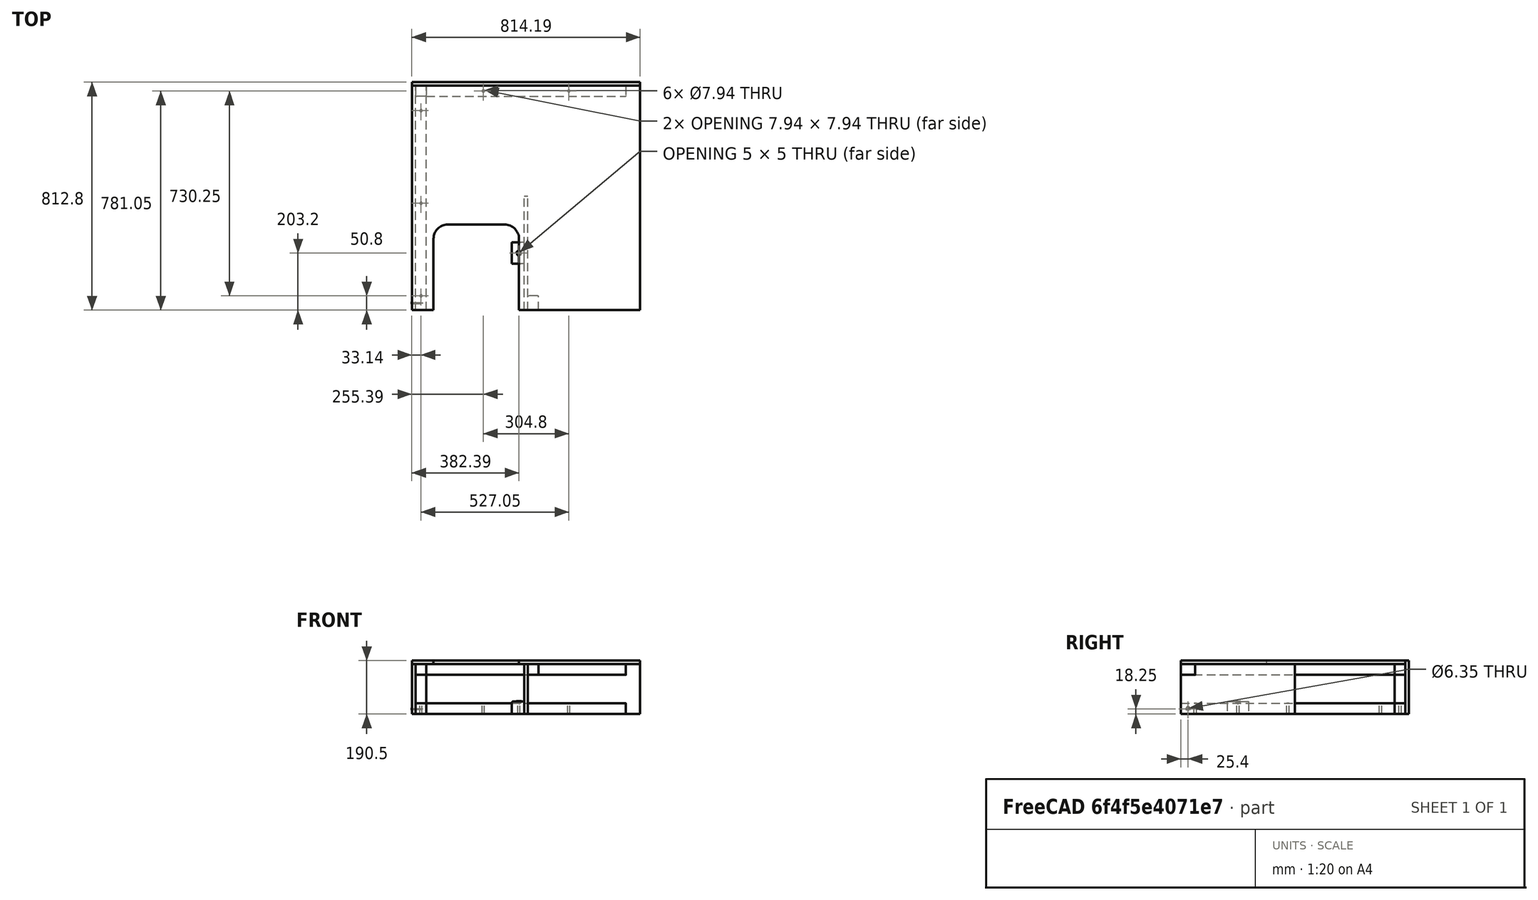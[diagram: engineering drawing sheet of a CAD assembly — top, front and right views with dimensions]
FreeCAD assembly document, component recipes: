
FREECAD ASSEMBLY — COMPONENT RECIPES ("Baffle_Box")

This assembly document has 66 components, labeled P0..P65 below (a component is one placed body or linked part). 0 of them carry a construction recipe — the FreeCAD feature program that regenerates the part from scratch, quoted from this document or its linked companion documents; the rest are supplied as boundary geometry only. No exploded tour is included for this assembly.
COMPONENT P0 — geometry summary ("Screw_w_Washer_A001"; no construction recipe available for this part):
  bounding box: 38.1 x 15.9 x 15.9 mm
  tessellated surface: 2,492 triangles
  volume: 527 mm^3 (5% of its bounding box)
  symmetry: mirror-symmetric across its y mid-plane, z mid-plane
COMPONENT P1 — geometry summary ("Part_F_Baffle_Side_Wall_002"; no construction recipe available for this part):
  bounding box: 800.1 x 177.8 x 12.7 mm
  tessellated surface: 12 triangles
  volume: 1806674 mm^3 (100% of its bounding box)
  symmetry: 2-fold rotationally symmetric about the x axis; 2-fold rotationally symmetric about the y axis; 2-fold rotationally symmetric about the z axis; mirror-symmetric across its x mid-plane, y mid-plane, z mid-plane
COMPONENT P2 — geometry summary ("BF_A001"; no construction recipe available for this part):
  bounding box: 800.1 x 38.1 x 38.1 mm
  tessellated surface: 220 triangles
  volume: 1154510 mm^3 (99% of its bounding box)
  symmetry: 2-fold rotationally symmetric about the x axis; 4-fold rotationally symmetric about the y axis; 2-fold rotationally symmetric about the z axis; mirror-symmetric across its x mid-plane, z mid-plane
COMPONENT P3 — geometry summary ("BF_B001"; no construction recipe available for this part):
  bounding box: 711.2 x 38.1 x 38.1 mm
  tessellated surface: 220 triangles
  volume: 1026231 mm^3 (99% of its bounding box)
  symmetry: 2-fold rotationally symmetric about the x axis; 2-fold rotationally symmetric about the y axis; 2-fold rotationally symmetric about the z axis; mirror-symmetric across its y mid-plane, z mid-plane
COMPONENT P4 — geometry summary ("BF_C001"; no construction recipe available for this part):
  bounding box: 139.7 x 38.1 x 38.1 mm
  tessellated surface: 220 triangles
  volume: 201581 mm^3 (99% of its bounding box)
  symmetry: 2-fold rotationally symmetric about the y axis; 4-fold rotationally symmetric about the z axis; mirror-symmetric across its y mid-plane, z mid-plane
COMPONENT P5 — geometry summary ("BF_E001"; no construction recipe available for this part):
  bounding box: 50.8 x 38.1 x 38.1 mm
  tessellated surface: 220 triangles
  volume: 73302 mm^3 (99% of its bounding box)
  symmetry: 4-fold rotationally symmetric about the y axis; 2-fold rotationally symmetric about the z axis; mirror-symmetric across its x mid-plane, y mid-plane
COMPONENT P6 — geometry summary ("Screw_w_Washer_A002"; no construction recipe available for this part):
  bounding box: 38.1 x 15.9 x 15.9 mm
  tessellated surface: 2,492 triangles
  volume: 527 mm^3 (5% of its bounding box)
  symmetry: mirror-symmetric across its y mid-plane, z mid-plane
COMPONENT P7 — geometry summary ("Screw_w_Washer_A003"; no construction recipe available for this part):
  bounding box: 38.1 x 15.9 x 15.9 mm
  tessellated surface: 2,492 triangles
  volume: 527 mm^3 (5% of its bounding box)
  symmetry: mirror-symmetric across its y mid-plane, z mid-plane
COMPONENT P8 — geometry summary ("Screw_w_Washer_A004"; no construction recipe available for this part):
  bounding box: 38.1 x 15.9 x 15.9 mm
  tessellated surface: 2,492 triangles
  volume: 527 mm^3 (5% of its bounding box)
  symmetry: mirror-symmetric across its y mid-plane, z mid-plane
COMPONENT P9 — geometry summary ("Screw_w_Washer_A005"; no construction recipe available for this part):
  bounding box: 38.1 x 15.9 x 15.9 mm
  tessellated surface: 2,492 triangles
  volume: 527 mm^3 (5% of its bounding box)
  symmetry: mirror-symmetric across its y mid-plane, z mid-plane
COMPONENT P10 — geometry summary ("Screw_w_Washer_A006"; no construction recipe available for this part):
  bounding box: 38.1 x 15.9 x 15.9 mm
  tessellated surface: 2,492 triangles
  volume: 527 mm^3 (5% of its bounding box)
  symmetry: mirror-symmetric across its y mid-plane, z mid-plane
COMPONENT P11 — geometry summary ("Screw_w_Washer_A007"; no construction recipe available for this part):
  bounding box: 38.1 x 15.9 x 15.9 mm
  tessellated surface: 2,492 triangles
  volume: 527 mm^3 (5% of its bounding box)
  symmetry: mirror-symmetric across its y mid-plane, z mid-plane
COMPONENT P12 — geometry summary ("Screw_w_Washer_A008"; no construction recipe available for this part):
  bounding box: 38.1 x 15.9 x 15.9 mm
  tessellated surface: 2,492 triangles
  volume: 527 mm^3 (5% of its bounding box)
  symmetry: mirror-symmetric across its y mid-plane, z mid-plane
COMPONENT P13 — geometry summary ("Screw_w_Washer_A009"; no construction recipe available for this part):
  bounding box: 38.1 x 15.9 x 15.9 mm
  tessellated surface: 2,492 triangles
  volume: 527 mm^3 (5% of its bounding box)
  symmetry: mirror-symmetric across its y mid-plane, z mid-plane
COMPONENT P14 — geometry summary ("Screw_w_Washer_A010"; no construction recipe available for this part):
  bounding box: 38.1 x 15.9 x 15.9 mm
  tessellated surface: 2,492 triangles
  volume: 527 mm^3 (5% of its bounding box)
  symmetry: mirror-symmetric across its y mid-plane, z mid-plane
COMPONENT P15 — geometry summary ("Screw_w_Washer_A011"; no construction recipe available for this part):
  bounding box: 38.1 x 15.9 x 15.9 mm
  tessellated surface: 2,492 triangles
  volume: 527 mm^3 (5% of its bounding box)
  symmetry: mirror-symmetric across its y mid-plane, z mid-plane
COMPONENT P16 — geometry summary ("Screw_w_Washer_A012"; no construction recipe available for this part):
  bounding box: 38.1 x 15.9 x 15.9 mm
  tessellated surface: 2,492 triangles
  volume: 527 mm^3 (5% of its bounding box)
  symmetry: mirror-symmetric across its y mid-plane, z mid-plane
COMPONENT P17 — geometry summary ("Screw_w_Washer_A013"; no construction recipe available for this part):
  bounding box: 38.1 x 15.9 x 15.9 mm
  tessellated surface: 2,492 triangles
  volume: 527 mm^3 (5% of its bounding box)
  symmetry: mirror-symmetric across its y mid-plane, z mid-plane
COMPONENT P18 — geometry summary ("Screw_w_Washer_A014"; no construction recipe available for this part):
  bounding box: 38.1 x 15.9 x 15.9 mm
  tessellated surface: 2,492 triangles
  volume: 527 mm^3 (5% of its bounding box)
  symmetry: mirror-symmetric across its y mid-plane, z mid-plane
COMPONENT P19 — geometry summary ("Screw_w_Washer_A015"; no construction recipe available for this part):
  bounding box: 38.1 x 15.9 x 15.9 mm
  tessellated surface: 2,492 triangles
  volume: 527 mm^3 (5% of its bounding box)
  symmetry: mirror-symmetric across its y mid-plane, z mid-plane
COMPONENT P20 — geometry summary ("Screw_w_Washer_A016"; no construction recipe available for this part):
  bounding box: 38.1 x 15.9 x 15.9 mm
  tessellated surface: 2,492 triangles
  volume: 527 mm^3 (5% of its bounding box)
  symmetry: mirror-symmetric across its y mid-plane, z mid-plane
COMPONENT P21 — geometry summary ("Screw_w_Washer_A017"; no construction recipe available for this part):
  bounding box: 38.1 x 15.9 x 15.9 mm
  tessellated surface: 2,492 triangles
  volume: 527 mm^3 (5% of its bounding box)
  symmetry: mirror-symmetric across its y mid-plane, z mid-plane
COMPONENT P22 — geometry summary ("Screw_w_Washer_A018"; no construction recipe available for this part):
  bounding box: 38.1 x 15.9 x 15.9 mm
  tessellated surface: 2,492 triangles
  volume: 527 mm^3 (5% of its bounding box)
  symmetry: mirror-symmetric across its y mid-plane, z mid-plane
COMPONENT P23 — geometry summary ("Screw_w_Washer_A019"; no construction recipe available for this part):
  bounding box: 38.1 x 15.9 x 15.9 mm
  tessellated surface: 2,492 triangles
  volume: 527 mm^3 (5% of its bounding box)
  symmetry: mirror-symmetric across its y mid-plane, z mid-plane
COMPONENT P24 — geometry summary ("Screw_w_Washer_A020"; no construction recipe available for this part):
  bounding box: 38.1 x 15.9 x 15.9 mm
  tessellated surface: 2,492 triangles
  volume: 527 mm^3 (5% of its bounding box)
  symmetry: mirror-symmetric across its y mid-plane, z mid-plane
COMPONENT P25 — geometry summary ("Screw_w_Washer_A021"; no construction recipe available for this part):
  bounding box: 38.1 x 15.9 x 15.9 mm
  tessellated surface: 2,492 triangles
  volume: 527 mm^3 (5% of its bounding box)
  symmetry: mirror-symmetric across its y mid-plane, z mid-plane
COMPONENT P26 — geometry summary ("Screw_w_Washer_A022"; no construction recipe available for this part):
  bounding box: 38.1 x 15.9 x 15.9 mm
  tessellated surface: 2,492 triangles
  volume: 527 mm^3 (5% of its bounding box)
  symmetry: mirror-symmetric across its y mid-plane, z mid-plane
COMPONENT P27 — geometry summary ("Screw_w_Washer_A023"; no construction recipe available for this part):
  bounding box: 38.1 x 15.9 x 15.9 mm
  tessellated surface: 2,492 triangles
  volume: 527 mm^3 (5% of its bounding box)
  symmetry: mirror-symmetric across its y mid-plane, z mid-plane
COMPONENT P28 — geometry summary ("Screw_w_Washer_A024"; no construction recipe available for this part):
  bounding box: 38.1 x 15.9 x 15.9 mm
  tessellated surface: 2,492 triangles
  volume: 527 mm^3 (5% of its bounding box)
  symmetry: mirror-symmetric across its y mid-plane, z mid-plane
COMPONENT P29 — geometry summary ("Screw_w_Washer_A025"; no construction recipe available for this part):
  bounding box: 38.1 x 15.9 x 15.9 mm
  tessellated surface: 2,492 triangles
  volume: 527 mm^3 (5% of its bounding box)
  symmetry: mirror-symmetric across its y mid-plane, z mid-plane
COMPONENT P30 — geometry summary ("Screw_w_Washer_A026"; no construction recipe available for this part):
  bounding box: 38.1 x 15.9 x 15.9 mm
  tessellated surface: 2,492 triangles
  volume: 527 mm^3 (5% of its bounding box)
  symmetry: mirror-symmetric across its y mid-plane, z mid-plane
COMPONENT P31 — geometry summary ("Screw_w_Washer_A027"; no construction recipe available for this part):
  bounding box: 38.1 x 15.9 x 15.9 mm
  tessellated surface: 2,492 triangles
  volume: 527 mm^3 (5% of its bounding box)
  symmetry: mirror-symmetric across its y mid-plane, z mid-plane
COMPONENT P32 — geometry summary ("Screw_w_Washer_A028"; no construction recipe available for this part):
  bounding box: 38.1 x 15.9 x 15.9 mm
  tessellated surface: 2,492 triangles
  volume: 527 mm^3 (5% of its bounding box)
  symmetry: mirror-symmetric across its y mid-plane, z mid-plane
COMPONENT P33 — geometry summary ("Screw_w_Washer_A029"; no construction recipe available for this part):
  bounding box: 38.1 x 15.9 x 15.9 mm
  tessellated surface: 2,492 triangles
  volume: 527 mm^3 (5% of its bounding box)
  symmetry: mirror-symmetric across its y mid-plane, z mid-plane
COMPONENT P34 — geometry summary ("Screw_w_Washer_A030"; no construction recipe available for this part):
  bounding box: 38.1 x 15.9 x 15.9 mm
  tessellated surface: 2,492 triangles
  volume: 527 mm^3 (5% of its bounding box)
  symmetry: mirror-symmetric across its y mid-plane, z mid-plane
COMPONENT P35 — geometry summary ("Screw_w_Washer_A031"; no construction recipe available for this part):
  bounding box: 38.1 x 15.9 x 15.9 mm
  tessellated surface: 2,492 triangles
  volume: 527 mm^3 (5% of its bounding box)
  symmetry: mirror-symmetric across its y mid-plane, z mid-plane
COMPONENT P36 — geometry summary ("Screw_w_Washer_A032"; no construction recipe available for this part):
  bounding box: 38.1 x 15.9 x 15.9 mm
  tessellated surface: 2,492 triangles
  volume: 527 mm^3 (5% of its bounding box)
  symmetry: mirror-symmetric across its y mid-plane, z mid-plane
COMPONENT P37 — geometry summary ("Screw_w_Washer_A033"; no construction recipe available for this part):
  bounding box: 38.1 x 15.9 x 15.9 mm
  tessellated surface: 2,492 triangles
  volume: 527 mm^3 (5% of its bounding box)
  symmetry: mirror-symmetric across its y mid-plane, z mid-plane
COMPONENT P38 — geometry summary ("Screw_w_Washer_A034"; no construction recipe available for this part):
  bounding box: 38.1 x 15.9 x 15.9 mm
  tessellated surface: 2,492 triangles
  volume: 527 mm^3 (5% of its bounding box)
  symmetry: mirror-symmetric across its y mid-plane, z mid-plane
COMPONENT P39 — geometry summary ("Screw_w_Washer_A035"; no construction recipe available for this part):
  bounding box: 38.1 x 15.9 x 15.9 mm
  tessellated surface: 2,492 triangles
  volume: 527 mm^3 (5% of its bounding box)
  symmetry: mirror-symmetric across its y mid-plane, z mid-plane
COMPONENT P40 — geometry summary ("Screw_w_Washer_A036"; no construction recipe available for this part):
  bounding box: 38.1 x 15.9 x 15.9 mm
  tessellated surface: 2,492 triangles
  volume: 527 mm^3 (5% of its bounding box)
  symmetry: mirror-symmetric across its y mid-plane, z mid-plane
COMPONENT P41 — geometry summary ("Screw_w_Washer_A037"; no construction recipe available for this part):
  bounding box: 38.1 x 15.9 x 15.9 mm
  tessellated surface: 2,492 triangles
  volume: 527 mm^3 (5% of its bounding box)
  symmetry: mirror-symmetric across its y mid-plane, z mid-plane
COMPONENT P42 — geometry summary ("Screw_w_Washer_A038"; no construction recipe available for this part):
  bounding box: 38.1 x 15.9 x 15.9 mm
  tessellated surface: 2,492 triangles
  volume: 527 mm^3 (5% of its bounding box)
  symmetry: mirror-symmetric across its y mid-plane, z mid-plane
COMPONENT P43 — geometry summary ("Screw_w_Washer_A039"; no construction recipe available for this part):
  bounding box: 38.1 x 15.9 x 15.9 mm
  tessellated surface: 2,492 triangles
  volume: 527 mm^3 (5% of its bounding box)
  symmetry: mirror-symmetric across its y mid-plane, z mid-plane
COMPONENT P44 — geometry summary ("Screw_w_Washer_A040"; no construction recipe available for this part):
  bounding box: 38.1 x 15.9 x 15.9 mm
  tessellated surface: 2,492 triangles
  volume: 527 mm^3 (5% of its bounding box)
  symmetry: mirror-symmetric across its y mid-plane, z mid-plane
COMPONENT P45 — geometry summary ("Screw_w_Washer_A041"; no construction recipe available for this part):
  bounding box: 38.1 x 15.9 x 15.9 mm
  tessellated surface: 2,492 triangles
  volume: 527 mm^3 (5% of its bounding box)
  symmetry: mirror-symmetric across its y mid-plane, z mid-plane
COMPONENT P46 — geometry summary ("Screw_w_Washer_A042"; no construction recipe available for this part):
  bounding box: 38.1 x 15.9 x 15.9 mm
  tessellated surface: 2,492 triangles
  volume: 527 mm^3 (5% of its bounding box)
  symmetry: mirror-symmetric across its y mid-plane, z mid-plane
COMPONENT P47 — geometry summary ("Screw_w_Washer_A043"; no construction recipe available for this part):
  bounding box: 38.1 x 15.9 x 15.9 mm
  tessellated surface: 2,492 triangles
  volume: 527 mm^3 (5% of its bounding box)
  symmetry: mirror-symmetric across its y mid-plane, z mid-plane
COMPONENT P48 — geometry summary ("Screw_w_Washer_A044"; no construction recipe available for this part):
  bounding box: 38.1 x 15.9 x 15.9 mm
  tessellated surface: 2,492 triangles
  volume: 527 mm^3 (5% of its bounding box)
  symmetry: mirror-symmetric across its y mid-plane, z mid-plane
COMPONENT P49 — geometry summary ("Screw_w_Washer_A045"; no construction recipe available for this part):
  bounding box: 38.1 x 15.9 x 15.9 mm
  tessellated surface: 2,492 triangles
  volume: 527 mm^3 (5% of its bounding box)
  symmetry: mirror-symmetric across its y mid-plane, z mid-plane
COMPONENT P50 — geometry summary ("Screw_w_Washer_A046"; no construction recipe available for this part):
  bounding box: 38.1 x 15.9 x 15.9 mm
  tessellated surface: 2,492 triangles
  volume: 527 mm^3 (5% of its bounding box)
  symmetry: mirror-symmetric across its y mid-plane, z mid-plane
COMPONENT P51 — geometry summary ("Cylinder001"; no construction recipe available for this part):
  bounding box: 50.8 x 7.9 x 7.9 mm
  tessellated surface: 252 triangles
  volume: 2514 mm^3 (79% of its bounding box)
  symmetry: 2-fold rotationally symmetric about the x axis; 2-fold rotationally symmetric about the y axis; revolution-symmetric about the z axis through its bounding-box center; mirror-symmetric across its x mid-plane, z mid-plane
COMPONENT P52 — geometry summary ("Cylinder002"; no construction recipe available for this part):
  bounding box: 50.8 x 7.9 x 7.9 mm
  tessellated surface: 252 triangles
  volume: 2514 mm^3 (79% of its bounding box)
  symmetry: 2-fold rotationally symmetric about the x axis; 2-fold rotationally symmetric about the y axis; revolution-symmetric about the z axis through its bounding-box center; mirror-symmetric across its x mid-plane, z mid-plane
COMPONENT P53 — geometry summary ("Cylinder003"; no construction recipe available for this part):
  bounding box: 50.8 x 7.9 x 7.9 mm
  tessellated surface: 252 triangles
  volume: 2514 mm^3 (79% of its bounding box)
  symmetry: 2-fold rotationally symmetric about the x axis; 2-fold rotationally symmetric about the y axis; revolution-symmetric about the z axis through its bounding-box center; mirror-symmetric across its x mid-plane, z mid-plane
COMPONENT P54 — geometry summary ("Baffle_Frame_D001"; no construction recipe available for this part):
  bounding box: 762.0 x 38.1 x 38.1 mm
  tessellated surface: 1,000 triangles
  volume: 1093877 mm^3 (99% of its bounding box)
  symmetry: 2-fold rotationally symmetric about the x axis; 2-fold rotationally symmetric about the z axis; mirror-symmetric across its x mid-plane, y mid-plane, z mid-plane
COMPONENT P55 — geometry summary ("T-Nut_1/005"; no construction recipe available for this part):
  bounding box: 18.0 x 18.0 x 9.0 mm
  tessellated surface: 1,636 triangles
  volume: 501 mm^3 (17% of its bounding box)
  symmetry: 4-fold rotationally symmetric about the z axis
COMPONENT P56 — geometry summary ("T-Nut_1/006"; no construction recipe available for this part):
  bounding box: 18.0 x 18.0 x 9.0 mm
  tessellated surface: 1,636 triangles
  volume: 501 mm^3 (17% of its bounding box)
  symmetry: 4-fold rotationally symmetric about the z axis
COMPONENT P57 — geometry summary ("T-Nut_1/007"; no construction recipe available for this part):
  bounding box: 18.0 x 18.0 x 9.0 mm
  tessellated surface: 1,636 triangles
  volume: 501 mm^3 (17% of its bounding box)
  symmetry: 4-fold rotationally symmetric about the z axis
COMPONENT P58 — geometry summary ("T-Nut_1/008"; no construction recipe available for this part):
  bounding box: 18.0 x 18.0 x 9.0 mm
  tessellated surface: 1,636 triangles
  volume: 501 mm^3 (17% of its bounding box)
  symmetry: 4-fold rotationally symmetric about the z axis
COMPONENT P59 — geometry summary ("T-Nut_1/009"; no construction recipe available for this part):
  bounding box: 18.0 x 18.0 x 9.0 mm
  tessellated surface: 1,636 triangles
  volume: 501 mm^3 (17% of its bounding box)
  symmetry: 4-fold rotationally symmetric about the z axis
COMPONENT P60 — geometry summary ("T-Nut_1/010"; no construction recipe available for this part):
  bounding box: 18.0 x 18.0 x 9.0 mm
  tessellated surface: 1,636 triangles
  volume: 501 mm^3 (17% of its bounding box)
  symmetry: 4-fold rotationally symmetric about the z axis
COMPONENT P61 — geometry summary ("Cylinder004"; no construction recipe available for this part):
  bounding box: 50.8 x 7.9 x 7.9 mm
  tessellated surface: 252 triangles
  volume: 2514 mm^3 (79% of its bounding box)
  symmetry: 2-fold rotationally symmetric about the x axis; 2-fold rotationally symmetric about the y axis; revolution-symmetric about the z axis through its bounding-box center; mirror-symmetric across its x mid-plane, z mid-plane
COMPONENT P62 — geometry summary ("Cylinder005"; no construction recipe available for this part):
  bounding box: 50.8 x 7.9 x 7.9 mm
  tessellated surface: 252 triangles
  volume: 2514 mm^3 (79% of its bounding box)
  symmetry: 2-fold rotationally symmetric about the x axis; 2-fold rotationally symmetric about the y axis; revolution-symmetric about the z axis through its bounding-box center; mirror-symmetric across its x mid-plane, z mid-plane
COMPONENT P63 — geometry summary ("T-Nut_1/011"; no construction recipe available for this part):
  bounding box: 18.0 x 18.0 x 9.0 mm
  tessellated surface: 1,636 triangles
  volume: 501 mm^3 (17% of its bounding box)
  symmetry: 4-fold rotationally symmetric about the z axis
COMPONENT P64 — geometry summary ("T-Nut_1/012"; no construction recipe available for this part):
  bounding box: 18.0 x 18.0 x 9.0 mm
  tessellated surface: 1,636 triangles
  volume: 501 mm^3 (17% of its bounding box)
  symmetry: 4-fold rotationally symmetric about the z axis
COMPONENT P65 — geometry summary ("Screw_w_Washer_A047"; no construction recipe available for this part):
  bounding box: 38.1 x 15.9 x 15.9 mm
  tessellated surface: 2,492 triangles
  volume: 527 mm^3 (5% of its bounding box)
  symmetry: mirror-symmetric across its y mid-plane, z mid-plane
PROVENANCE & LICENSES
A FreeCAD (.FCStd) document from a public repository crawl; recipes are the document's own serialized feature recipes (and, for linked parts, companion documents' recipes).
License: gpl-3.0.
